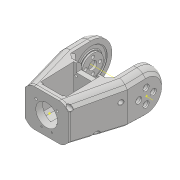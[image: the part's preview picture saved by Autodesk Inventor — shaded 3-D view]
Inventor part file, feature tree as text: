
AUTODESK INVENTOR PART (.ipt)
format: ipt  version: 2018 (Build 220112000, 112)  size: 1,141,760 bytes
history: native  units: mm
features: projected_geometry x49, sketch x46, extrude x38, hole x13, fillet x11, other x10, chamfer x6, reference x3, mirror x1, plane x1
ambient origin geometry x8: Origin, YZ Plane, XZ Plane, XY Plane, X Axis, Y Axis, Z Axis, Center Point
bodies: Solid1 (feature_tree)
feature tree (178):
  extrude  "Extrusion1"  Depth=45.0mm
  extrude  "Extrusion2"  Depth=2.25mm
  hole  "Hole1"  [1 undecoded]
  hole  "Hole2"  [1 undecoded]
  fillet  "Fillet1"  Radius=14.0mm
  extrude  "Extrusion3"  Depth=18.5mm
  extrude  "Extrusion4"  Depth=20.5mm
  extrude  "Extrusion5"  Depth=2.195mm
  extrude  "Extrusion6"  Depth=20.5mm
  hole  "Hole3"  [1 undecoded]
  extrude  "Extrusion7"  Depth=0.5mm
  extrude  "Extrusion8"  Depth=1.0mm TaperAngle=0.0deg
  extrude  "Extrusion9"  Depth=24.5mm
  extrude  "Extrusion10"  Depth=10.0mm
  extrude  "Extrusion11"  Depth=14.5mm
  extrude  "Extrusion13"  Depth=14.5mm
  extrude  "Extrusion14"  Depth=5.0mm
  extrude  "Extrusion15"  Depth=2.25mm
  extrude  "Extrusion16"  Depth=5.0mm
  extrude  "Extrusion17"  Depth=9.0mm
  chamfer  "Chamfer1"  Distance=1.0mm
  fillet  "Fillet7"  Radius=20.7mm
  fillet  "Fillet8"  Radius=32.0mm
  mirror  "Mirror1"
  sketch  "Sketch26"  dims[d55=2.25mm d56=5.0mm]
  extrude  "Extrusion24"  Depth=1.0mm TaperAngle=0.0deg
  extrude  "Extrusion25"  Depth=8.0mm
  extrude  "Extrusion26"  Depth=0.2mm TaperAngle=0.0deg
  extrude  "Extrusion27"  Depth=5.0mm TaperAngle=0.0deg
  other  "Work Axis1"
  plane  "Work Plane2"
  extrude  "Extrusion28"  Depth=0.2mm TaperAngle=0.0deg
  extrude  "Extrusion29"  Depth=2.5mm TaperAngle=45.0deg
  extrude  "Extrusion31"  Depth=0.5mm
  extrude  "Extrusion32"  Depth=36.0mm
  extrude  "Extrusion33"  Depth=60.0mm
  sketch  "Sketch41"  dims[d100=0.2mm d101=0.0mm d102=2.5mm d103=2.0mm d104=45.0deg]
  extrude  "Extrusion34"  Depth=2.3mm
  chamfer  "Chamfer6"  Distance=15.0mm
  fillet  "Fillet9"  Radius=15.0mm
  extrude  "Extrusion35"  Depth=15.0mm TaperAngle=0.0deg
  extrude  "Extrusion36"  Depth=41.5mm
  fillet  "Fillet10"  Radius=15.5mm
  extrude  "Extrusion37"  Depth=5.0mm
  extrude  "Extrusion38"  Depth=100.0mm TaperAngle=0.0deg
  extrude  "Extrusion39"  Depth=11.5mm
  extrude  "Extrusion40"  Depth=11.5mm
  hole  "Hole6"  [1 undecoded]
  fillet  "Fillet12"  Radius=100.0mm
  extrude  "Extrusion41"  Depth=100.0mm TaperAngle=0.0deg
  extrude  "Extrusion42"  Depth=8.0mm
  hole  "Hole7"  [1 undecoded]
  extrude  "Extrusion43"  Depth=1.0mm TaperAngle=0.0deg
  extrude  "Extrusion44"  Depth=0.3mm
  sketch  "Sketch58"  dims[d202=15.0deg d204=10.970628mm]
  hole  "Hole8"  [1 undecoded]
  hole  "Hole9"  [1 undecoded]
  hole  "Hole10"  [1 undecoded]
  hole  "Hole11"  [1 undecoded]
  hole  "Hole12"  [1 undecoded]
  hole  "Hole13"  [1 undecoded]
  hole  "Hole14"  [1 undecoded]
  hole  "Hole15"  [1 undecoded]
  chamfer  "Chamfer10"  Distance=0.75mm
  chamfer  "Chamfer11"  Distance=20.5mm
  chamfer  "Chamfer12"  Distance=3.05mm
  chamfer  "Chamfer13"  Distance=14.0mm
  extrude  "Extrusion45"  Depth=0.3mm
  fillet  "Fillet13"  Radius=1.55mm
  extrude  "Extrusion46"  Depth=0.3mm
  fillet  "Fillet14"  Radius=2.5mm
  fillet  "Fillet15"  Radius=8.0mm
  fillet  "Fillet16"  Radius=2.5mm
  fillet  "Fillet17"  Radius=4.624622mm
  sketch  "Sketch1"  dims[d0=24.5mm d1=45.0mm]
  sketch  "Sketch2"  dims[d2=1.95mm d3=0.0mm d4=2.25mm]
  projected_geometry  "Projected Loop1"
  sketch  "Sketch3"  dims[d5=20.0mm d6=2.25mm]
  projected_geometry  "Projected Loop2"
  sketch  "Sketch4"  dims[d7=5.25mm d8=5.25mm d9=14.0mm]
  projected_geometry  "Projected Loop3"
  sketch  "Sketch5"  dims[d10=5.25mm d11=18.5mm]
  projected_geometry  "Projected Loop4"
  sketch  "Sketch6"  dims[d12=10.0mm d13=0.0mm d14=20.5mm]
  projected_geometry  "Projected Loop5"
  sketch  "Sketch7"  dims[d15=2.0mm d16=2.195mm]
  projected_geometry  "Projected Loop6"
  sketch  "Sketch8"  dims[d17=2.0mm]
  projected_geometry  "Projected Loop7"
  sketch  "Sketch9"  dims[d18=2.4mm d19=6.0mm d20=4.4mm d21=2.0mm d22=90.0deg d23=8.0mm d24=20.594885mm d25=20.5mm]
  projected_geometry  "Projected Loop8"
  projected_geometry  "Projected Loop9"
  sketch  "Sketch10"  dims[d26=26.65mm d27=2.0mm]
  projected_geometry  "Projected Loop10"
  projected_geometry  "Projected Loop11"
  sketch  "Sketch11"  dims[d28=2.0mm]
  projected_geometry  "Projected Loop12"
  sketch  "Sketch12"  dims[d29=2.4mm d30=6.0mm d31=4.4mm d32=2.0mm d33=90.0deg d34=8.0mm d35=20.594885mm d36=0.5mm]
  sketch  "Sketch13"  dims[d37=18.0mm d38=1.0mm d39=0.0mm]
  sketch  "Sketch14"  dims[d41=5.0mm d42=0.0mm d43=24.5mm]
  projected_geometry  "Projected Loop13"
  sketch  "Sketch16"  dims[d44=1.15mm d45=0.0mm d46=10.0mm]
  projected_geometry  "Projected Loop14"
  sketch  "Sketch17"  dims[d47=21.0mm d48=14.5mm]
  projected_geometry  "Projected Loop15"
  sketch  "Sketch18"  dims[d49=20.0mm d50=14.5mm]
  projected_geometry  "Projected Loop16"
  sketch  "Sketch19"  dims[d51=24.5mm d52=5.0mm]
  projected_geometry  "Projected Loop17"
  sketch  "Sketch20"  dims[d53=5.0mm d54=2.25mm]
  projected_geometry  "Projected Loop18"
  projected_geometry  "Projected Loop25"
  sketch  "Sketch31"  dims[d57=5.0mm d58=9.0mm]
  projected_geometry  "Projected Loop30"
  reference  "Reference1"
  sketch  "Sketch32"  dims[d59=14.75mm]
  projected_geometry  "Projected Loop31"
  sketch  "Sketch33"  dims[d60=4.0mm d61=1.0mm d62=0.0mm d63=20.7mm]
  projected_geometry  "Projected Loop32"
  sketch  "Sketch34"  dims[d64=2.3mm d65=6.0mm d66=4.4mm d67=2.0mm d68=90.0deg d69=8.0mm d70=20.594885mm d72=32.0mm]
  projected_geometry  "Projected Loop33"
  other  "Work Point1"
  other  "Work Point2"
  other  "Work Point3"
  sketch  "Sketch35"  dims[d73=3.0mm d74=0.0mm d75=1.0mm d76=0.0mm]
  sketch  "Sketch37"  dims[d77=12.25mm d78=0.0mm d80=8.0mm]
  projected_geometry  "Projected Loop34"
  sketch  "Sketch38"  dims[d81=4.5mm d82=0.0mm d84=0.2mm d85=0.0mm]
  sketch  "Sketch39"  dims[d91=8.0mm d92=0.0mm d93=5.0mm d94=0.0mm]
  sketch  "Sketch40"  dims[d95=5.0mm d96=0.0mm d98=0.2mm d99=0.0mm]
  projected_geometry  "Projected Loop35"
  projected_geometry  "Projected Loop36"
  projected_geometry  "Projected Loop37"
  projected_geometry  "Projected Loop38"
  sketch  "Sketch42"  dims[d105=1.5mm d114=0.5mm]
  projected_geometry  "Projected Loop39"
  sketch  "Sketch43"  dims[d130=60.0mm d131=36.0mm]
  reference  "Reference2"
  reference  "Reference3"
  sketch  "Sketch45"  dims[d146=40.0mm d147=60.0mm]
  projected_geometry  "Projected Loop40"
  sketch  "Sketch46"  dims[d148=0.0mm d149=2.3mm d150=15.0mm d151=0.0mm d152=15.0mm d153=0.0mm]
  projected_geometry  "Projected Loop41"
  sketch  "Sketch48"  dims[d154=15.0mm d155=0.0mm d156=15.0mm d157=0.0mm]
  projected_geometry  "Projected Loop43"
  sketch  "Sketch49"  dims[d158=20.5mm d159=41.5mm d160=15.5mm]
  projected_geometry  "Projected Loop44"
  projected_geometry  "Projected Loop45"
  sketch  "Sketch50"  dims[d161=15.5mm d162=5.0mm]
  projected_geometry  "Projected Loop46"
  sketch  "Sketch52"  dims[d165=100.0mm d166=0.0mm d167=100.0mm d168=0.0mm]
  sketch  "Sketch53"  dims[d172=0.0mm d173=11.5mm]
  projected_geometry  "Projected Loop47"
  sketch  "Sketch54"  dims[d175=11.5mm d176=11.5mm]
  projected_geometry  "Projected Loop48"
  sketch  "Sketch55"  dims[d179=100.0mm d180=0.0mm d187=7.0mm d188=100.0mm d189=0.0mm]
  sketch  "Sketch56"  dims[d193=100.0mm d194=0.0mm d195=100.0mm d196=0.0mm]
  projected_geometry  "Projected Loop49"
  sketch  "Sketch57"  dims[d197=5.0mm d198=2.0mm d199=45.0deg d200=8.0mm]
  projected_geometry  "Projected Loop50"
  projected_geometry  "Projected Loop51"
  projected_geometry  "Projected Loop52"
  projected_geometry  "Projected Loop53"
  projected_geometry  "Projected Loop55"
  projected_geometry  "Projected Loop56"
  projected_geometry  "Projected Loop57"
  sketch  "Sketch59"  dims[d205=15.470628mm d206=1.0mm d207=0.0mm]
  projected_geometry  "Projected Loop58"
  sketch  "Sketch60"  dims[d208=1.0mm d209=0.0mm d213=2.0mm d215=15.0deg d216=4.0mm d217=4.0mm d218=5.0mm d219=0.0mm d222=32.0mm d223=4.0mm d224=0.0mm d225=2.5mm d226=0.0mm d227=6.5mm d228=0.0mm d235=1.567mm d236=15.0mm d237=4.0mm d238=2.0mm d239=90.0deg d240=15.0mm d241=20.594885mm d243=0.75mm d244=20.5mm d245=3.05mm d246=0.0mm d247=14.0mm d248=3.2mm d249=6.0mm d250=4.0mm d251=2.0mm d252=90.0deg d253=8.8mm d254=20.594885mm d255=20.5mm d256=1.55mm d257=0.0mm d258=8.0mm d259=2.5mm d260=0.0mm d261=8.0mm d262=2.5mm d263=0.0mm d266=4.624622mm d267=4.624622mm d268=2.75mm d269=2.75mm d270=2.35mm d271=2.35mm d272=14.0mm d273=4.0mm d274=5.6mm d275=3.708mm d276=3.023mm d277=2.0mm d278=14.3117mm d279=17.0mm d280=0.0mm d281=4.0mm d282=3.708mm d283=3.023mm d284=2.0mm d285=14.3117mm d286=19.0mm d287=0.0mm d288=4.0mm d289=3.708mm d290=3.023mm d291=2.0mm d292=14.3117mm d293=20.0mm d294=0.0mm d295=2.3mm d296=4.0mm d297=4.4mm d298=2.0mm d299=90.0deg d300=32.25mm d301=0.0mm d302=3.3mm d303=4.0mm d304=6.3mm d305=2.0mm d306=90.0deg d307=32.25mm d308=0.0mm d309=1.567mm d310=4.0mm d311=6.3mm d312=2.0mm d313=90.0deg d314=45.0mm d315=20.594885mm d316=1.567mm d317=4.0mm d318=6.3mm d319=2.0mm d320=90.0deg d321=55.0mm d322=20.594885mm d323=2.459mm d324=6.0mm d325=6.3mm d326=2.0mm d327=90.0deg d328=50.0mm d329=20.594885mm d330=3.0mm d331=2.0mm d332=45.0deg d333=5.0mm d334=20.0mm d335=45.0deg d336=5.0mm d337=20.0mm d338=45.0deg d339=5.0mm d340=20.0mm d341=45.0deg d342=6.0mm d343=6.0mm d344=6.0mm d345=6.0mm d346=2.0mm d347=0.0mm d348=1.5mm d349=6.0mm d350=6.0mm d351=6.0mm d352=6.0mm d353=3.0mm d354=0.0mm d355=1.5mm d356=0.4mm d357=0.4mm d358=0.3mm]
  projected_geometry  "Projected Loop59"
  parser-record x1  (decoder bookkeeping rows leaked as tree rows — omitted from the tree; the rows remain in map.json)
  other  "servocheck.iam"
  other  "LX-16A:3"
  other  "DUOPAN-SG-SJ_10"
  projected_geometry  "Project Cut Edges1"
  projected_geometry  "Project Cut Edges3"
  other  "bottomarm:1"
  other  "arm1:1"
note: 13 required parameter values undecoded (feature->parameter linkage not recoverable at this tier; creation-order binding heuristic only, values carry confidence <= 0.55)
note: 1 file-system path scrubbed to <path> (originals preserved in map.json)
